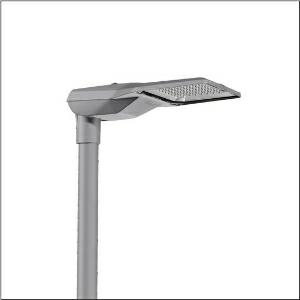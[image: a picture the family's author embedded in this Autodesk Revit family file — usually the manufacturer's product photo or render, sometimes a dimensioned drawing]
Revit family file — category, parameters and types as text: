
# Revit family: streetlight_sl_21_midi___st0_5a_5xe3b43s08nb_c2ea
name_source: partatom
category: Lighting Fixtures
units: mm (PartAtom-declared; Revit-internal decimal feet)

## family parameters
Cut with Voids When Loaded = No
Host = Face
Light Source = No
Part Type = Normal
Room Calculation Point = No
Round Connector Dimension = Use Diameter
Shared = No

## types (1)
- --- (1 x LED, 23710 lm, 151.2 W, 4000K)
    Apparent Load = 151 VA
    CIE Flux Codes = 43 76 97 100 100
    Color Rendering = 70
    Color Temperature = 4000K
    Default Elevation = 1800 mm
    Description = Streetlight SL 21 midi, mast luminaire, primary light control with lens, of PMMA, primary optical cover: cover, of toughened safety glass, transparent, light distribution: ST0.5a, light emission: direct distribution, primary light characteristic: asymmetric, installation type: side-entry, post-top, LED, High Power LED, rated luminous flux: 23.710lm, luminous efficacy: 157lm/W, light colour: 740, colour temperature: 4000K, control gear: D4i, control: overheat protection, constant luminous flux control, time-dependent luminous flux control, flexible luminous flux parameterisation, pre-setting: logarithmic dimming characteristic, mains connection: 230..240V, AC, 50/60Hz, start of lifetime: 151W, end of service life: 157W, reduction: 70W, luminaire housing, of diecast aluminium, powder-coated, SITECO metallic grey (DB 702S), corrosivity category C5 high according to DIN EN ISO 12944, please order mast flange separately, inclination adjustable: 0°, 5°, 10°, 15°, sealing non-destructively replaceable, multi-level sealing system, length: 644mm, width: 335mm, height: 110mm, mast flange for spigot size: 42mm (side-entry): 5XC10008XM4, 60/48mm (side-entry/post-top): 5XC10108XM2, 76/60mm (side-entry/post-top): 5XC10108XM1, mounting height: 4..8m, Smart Interface above, protection rating (complete): IP66, insulation class (complete): insulation class II (safety insulation), certification: CE, ENEC, ENEC+, VDE, impact resistance: IK10, permissible operating ambient temperature for outdoor applications: -40..+50°C, standard-compliant lighting for roads and squares, packaging unit: 1 piece

Light Distribution: ST0.5a
    Height = 111 mm
    Lamp = 1 x LED
    Lamp Light Flux = 23710 lm
    Lamp Power = 151.2 W
    Lamp count = 1
    Length = 644 mm
    Luminous efficacy = 157 lm/W
    Manufacturer = Siteco
    ModVariant = No
    Model = 5XE3B43S08NB
    Number of Poles = 1
    OnlyDefault = Yes
    Power Factor = 1
    Product Name = Streetlight SL 21 midi | ST0.5a
    Product group = mast luminaire | pylon top
    ProductGroupID = 6100
    Protection Class = Protection class II
    Protection Degree = IP 66
    RLX_Detail_Level = 1
    RLX_Emergency_Light_Flux = 0 lm
    RLX_Emergency_Type = 0
    RLX_Emergency_Type_DB = No
    RlxData = <blob elided: 38165 chars, md5=ac467479>
    Socket = socket
    Standby Power = 0 W
    System Light Flux = 23710 lm
    System Power = 151 W
    Type Comments = factory setting: luminous flux: 100 % | dim-lin: 254 | 802 mA
    Type Image = l_1004302.jpg
    URL = http://relux.com
    VarID = @adj_170867
    Voltage = 0 V
    Weight = 0.00 kg
    Width = 336 mm

## geometry (parser evidence)
native form markers: Blend x4, Sweep x9
no freeform markers — native parametric forms only
